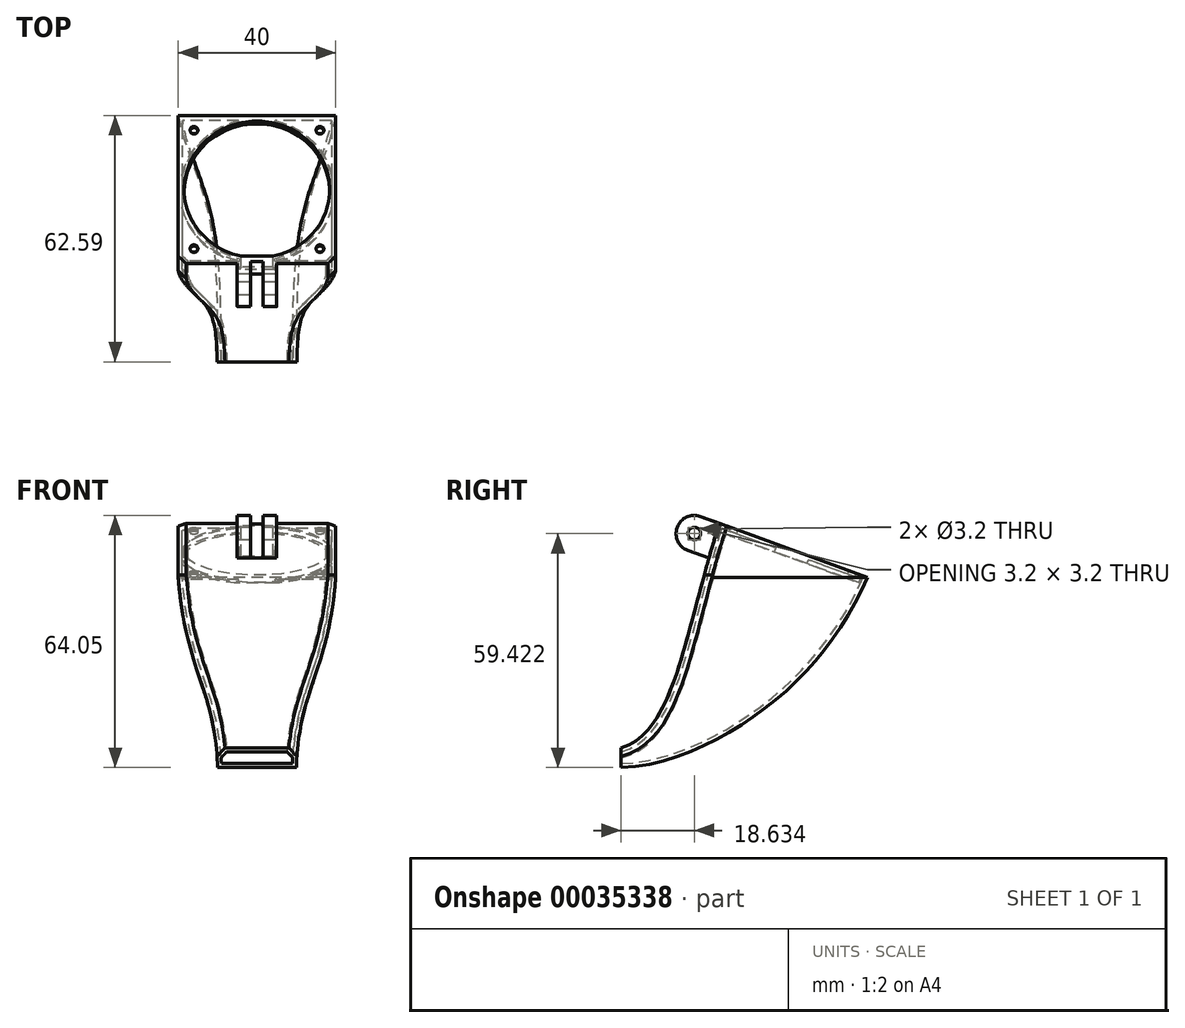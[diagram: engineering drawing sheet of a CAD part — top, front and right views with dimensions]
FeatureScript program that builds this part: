
annotation { "Feature Type Name" : "Feature", "Feature Type Description" : "" }
export const myFeature = defineFeature(function(context is Context, id is Id, definition is map)
    precondition{}
    {
        {
            var Q0;
            Q0=qCreatedBy(makeId("Right.planeOp"),FACE);
            var sketch = newSketch(context, id + "F0", { "sketchPlane" : qUnion([Q0])});
            skLineSegment(sketch, "E0", {"start": v(0, 5) * mm, "end": v(0, 0) * mm});
            skLineSegment(sketch, "E1", {"start": v(62.59, 48.32) * mm, "end": v(25, 62) * mm});
            skFitSpline(sketch, "E2", {"points": [v(62.59, 48.32) * mm, v(0, 0) * mm], "startDerivative": vector(-40.57, -96.87) * mm, "endDerivative": vector(-50.06, 0) * mm});
            skFitSpline(sketch, "E3", {"points": [v(25, 62) * mm, v(0, 5) * mm], "startDerivative": vector(-26.25, -81.63) * mm, "endDerivative": vector(-41.59, -11.88) * mm});
            skSolve(sketch);
        }
        {
            var Q0;
            Q0=qSketchRegion(id+"F0",true);
            extrude(context, id + "F1", {"entities" : qUnion([Q0]), "depth" : 40 * mm, "symmetric" : true});
        }
        {
            var Q0;
            Q0=qCreatedBy(makeId("Front.planeOp"),FACE);
            var sketch = newSketch(context, id + "F2", { "sketchPlane" : qUnion([Q0])});
            skLineSegment(sketch, "E4", {"start": v(10, 0) * mm, "end": v(-10, 0) * mm});
            skLineSegment(sketch, "E5", {"start": v(20, 62) * mm, "end": v(-20, 62) * mm});
            skLineSegment(sketch, "E6", {"start": v(-20, 62) * mm, "end": v(-20, 48.32) * mm});
            skLineSegment(sketch, "E7", {"start": v(20, 62) * mm, "end": v(20, 48.32) * mm});
            skPoint(sketch, "E8", {"position": v(0, 0) * mm});
            skFitSpline(sketch, "E9", {"points": [v(20, 48.32) * mm, v(10, 0) * mm], "startDerivative": vector(-5.16, -71.52) * mm, "endDerivative": vector(-1.89, -60.47) * mm});
            skFitSpline(sketch, "E10.0.MirrorCS", {"points": [v(-20, 48.32) * mm, v(-10, 0) * mm], "startDerivative": vector(5.16, -71.52) * mm, "endDerivative": vector(1.89, -60.47) * mm});
            skSolve(sketch);
        }
        {
            var Q0;
            Q0=qSketchRegion(id+"F2",true);
            var Q1;
            Q1=makeQuery(id+"F1.opExtrude","SWEPT_FACE",FACE,{"disambiguationData":[OSD([sQuery(id+"F0.wireOp",EDGE,"E2")])]});
            extrude(context, id + "F3", {"entities" : qUnion([Q0]), "operationType" : NewBodyOperationType.INTERSECT, "endBound" : BoundingType.UP_TO_BODY, "oppositeDirection" : true, "endBoundEntityBody" : qUnion([Q1]), "depth" : 25 * mm});
        }
        {
            var Q0;
            Q0=makeQuery(id+"F1.opExtrude","SWEPT_FACE",FACE,{"disambiguationData":[OSD([sQuery(id+"F0.wireOp",EDGE,"E1")])]});
            var sketch = newSketch(context, id + "F4", { "sketchPlane" : qUnion([Q0])});
            skLineSegment(sketch, "E11", {"start": v(20, 2.29) * mm, "end": v(-20, 42.29) * mm, "construction": true});
            skLineSegment(sketch, "E12", {"start": v(-20, 2.29) * mm, "end": v(20, 42.29) * mm, "construction": true});
            skCircle(sketch, "E13", {"center": v(0, 22.29) * mm, "radius": 18.5 * mm});
            skSolve(sketch);
        }
        {
            var Q0;
            Q0=qSketchRegion(id+"F4",true);
            extrude(context, id + "F5", {"entities" : qUnion([Q0]), "operationType" : NewBodyOperationType.REMOVE, "oppositeDirection" : true, "depth" : 2 * mm});
        }
        {
            var Q0;
            Q0=makeQuery(id+"F3.boolean.opBoolean","COPY",EDGE,{"derivedFrom":makeQuery(id+"F3.opExtrude","TWEAK_EDGE",EDGE,{"derivedFrom":[makeQuery(id+"F1.opExtrude","SWEPT_FACE",FACE,{"disambiguationData":[OSD([sQuery(id+"F0.wireOp",EDGE,"E2")])]}),makeQuery(id+"F2.imprint","IMPRINT",EDGE,{"derivedFrom":sQuery(id+"F2.wireOp",EDGE,"E9")})]})});
            var Q1;
            Q1=makeQuery(id+"F3.boolean.opBoolean","INTERSECT",EDGE,{"derivedFrom":[makeQuery(id+"F1.opExtrude","SWEPT_FACE",FACE,{"disambiguationData":[OSD([sQuery(id+"F0.wireOp",EDGE,"E3")])]}),makeQuery(id+"F3.opExtrude","SWEPT_FACE",FACE,{"disambiguationData":[OSD([sQuery(id+"F2.wireOp",EDGE,"E9")])]})]});
            var Q2;
            Q2=makeQuery(id+"F1.opExtrude","CAP_EDGE",EDGE,{"disambiguationData":[OSD([sQuery(id+"F0.wireOp",EDGE,"E3")])],"isStart":false});
            var Q3;
            Q3=makeQuery(id+"F3.boolean.opBoolean","INTERSECT",EDGE,{"derivedFrom":[makeQuery(id+"F1.opExtrude","SWEPT_FACE",FACE,{"disambiguationData":[OSD([sQuery(id+"F0.wireOp",EDGE,"E3")])]}),makeQuery(id+"F3.opExtrude","SWEPT_FACE",FACE,{"disambiguationData":[OSD([sQuery(id+"F2.wireOp",EDGE,"E10.0.MirrorCS")])]})]});
            var Q4;
            Q4=makeQuery(id+"F1.opExtrude","CAP_EDGE",EDGE,{"disambiguationData":[OSD([sQuery(id+"F0.wireOp",EDGE,"E3")])],"isStart":true});
            var Q5;
            Q5=makeQuery(id+"F3.boolean.opBoolean","COPY",EDGE,{"derivedFrom":makeQuery(id+"F3.opExtrude","TWEAK_EDGE",EDGE,{"derivedFrom":[makeQuery(id+"F1.opExtrude","SWEPT_FACE",FACE,{"disambiguationData":[OSD([sQuery(id+"F0.wireOp",EDGE,"E2")])]}),makeQuery(id+"F2.imprint","IMPRINT",EDGE,{"derivedFrom":sQuery(id+"F2.wireOp",EDGE,"E10.0.MirrorCS")})]})});
            chamfer(context, id + "F6", {"entities" : qUnion([Q0, Q1, Q2, Q3, Q4, Q5]), "width" : 2 * mm, "tangentPropagation" : true});
        }
        {
            var Q0;
            Q0=makeQuery(id+"F5.boolean.opBoolean","COPY",FACE,{"derivedFrom":makeQuery(id+"F5.opExtrude","CAP_FACE",FACE,{"disambiguationData":[OSD([sQuery(id+"F4.wireOp",EDGE,"E13")])],"isStart":false})});
            var Q1;
            Q1=makeQuery(id+"F1.opExtrude","SWEPT_FACE",FACE,{"disambiguationData":[OSD([sQuery(id+"F0.wireOp",EDGE,"E0")])]});
            shell(context, id + "F7", {"entities" : qUnion([Q0, Q1]), "thickness" : 1 * mm});
        }
        {
            var Q0;
            Q0=makeQuery(id+"F1.opExtrude","SWEPT_FACE",FACE,{"disambiguationData":[OSD([sQuery(id+"F0.wireOp",EDGE,"E1")])]});
            var sketch = newSketch(context, id + "F8", { "sketchPlane" : qUnion([Q0])});
            skCircle(sketch, "E14", {"center": v(16, 38.34) * mm, "radius": 1 * mm});
            skCircle(sketch, "E15", {"center": v(-16, 38.34) * mm, "radius": 1 * mm});
            skCircle(sketch, "E16", {"center": v(-16, 6.34) * mm, "radius": 1 * mm});
            skCircle(sketch, "E17", {"center": v(16, 6.34) * mm, "radius": 1 * mm});
            skPoint(sketch, "E18", {"position": v(-20, 22.34) * mm});
            skSolve(sketch);
        }
        {
            var Q0;
            Q0=qSketchRegion(id+"F8",true);
            var Q1;
            Q1=makeQuery(id+"F7.opShell","OFFSET_FACE",FACE,{"disambiguationData":[OSD([sQuery(id+"F0.wireOp",EDGE,"E1")]),OD(1.0)]});
            extrude(context, id + "F9", {"entities" : qUnion([Q0]), "operationType" : NewBodyOperationType.REMOVE, "endBound" : BoundingType.UP_TO_SURFACE, "oppositeDirection" : true, "endBoundEntityFace" : qUnion([Q1]), "depth" : 25 * mm});
        }
        {
            var Q0;
            Q0=qCreatedBy(makeId("Right.planeOp"),FACE);
            var sketch = newSketch(context, id + "F10", { "sketchPlane" : qUnion([Q0])});
            skLineSegment(sketch, "E19", {"start": v(15.88, 65.32) * mm, "end": v(12.74, 56.67) * mm});
            skLineSegment(sketch, "E20", {"start": v(12.74, 56.67) * mm, "end": v(23.73, 52.67) * mm});
            skLineSegment(sketch, "E21", {"start": v(23.73, 52.67) * mm, "end": v(26.88, 61.32) * mm});
            skLineSegment(sketch, "E22", {"start": v(26.88, 61.32) * mm, "end": v(25, 62) * mm});
            skLineSegment(sketch, "E23", {"start": v(25, 62) * mm, "end": v(25, 62) * mm});
            skLineSegment(sketch, "E24", {"start": v(25, 62) * mm, "end": v(15.88, 65.32) * mm});
            skCircle(sketch, "E25", {"center": v(18.63, 59.42) * mm, "radius": 1.6 * mm});
            skSolve(sketch);
        }
        {
            var Q0;
            Q0=qSketchRegion(id+"F10",true);
            extrude(context, id + "F11", {"entities" : qUnion([Q0]), "operationType" : NewBodyOperationType.ADD, "depth" : 10 * mm, "symmetric" : true});
        }
        {
            var Q0;
            Q0=makeQuery(id+"F11.opExtrude","CAP_EDGE",EDGE,{"disambiguationData":[OSD([sQuery(id+"F10.wireOp",EDGE,"E21")])],"isStart":true});
            var Q1;
            Q1=makeQuery(id+"F11.opExtrude","CAP_EDGE",EDGE,{"disambiguationData":[OSD([sQuery(id+"F10.wireOp",EDGE,"E21")])],"isStart":false});
            var Q2;
            Q2=makeQuery(id+"F11.opExtrude","SWEPT_EDGE",EDGE,{"disambiguationData":[OSD([sQuery(id+"F10.wireOp",EDGE,"E20"),sQuery(id+"F10.wireOp",EDGE,"E21")])]});
            chamfer(context, id + "F12", {"entities" : qUnion([Q0, Q1, Q2]), "width" : 1 * mm, "tangentPropagation" : true});
        }
        {
            var Q0;
            Q0=makeQuery(id+"F11.opExtrude","SWEPT_EDGE",EDGE,{"disambiguationData":[OSD([sQuery(id+"F10.wireOp",EDGE,"E19"),sQuery(id+"F10.wireOp",EDGE,"E20")])]});
            var Q1;
            Q1=makeQuery(id+"F11.opExtrude","SWEPT_EDGE",EDGE,{"disambiguationData":[OSD([sQuery(id+"F10.wireOp",EDGE,"E19"),sQuery(id+"F10.wireOp",EDGE,"E24")])]});
            fillet(context, id + "F13", {"entities" : qUnion([Q0, Q1]), "radius" : 4.5 * mm, "tangentPropagation" : true, "allowEdgeOverflow" : false});
        }
        {
            var Q0;
            {var subQ0=sQuery(id+"F10.wireOp",EDGE,"E20");Q0=makeQuery(id+"F11.boolean.opBoolean","SPLIT",FACE,{"disambiguationData":[TD([makeQuery(id+"F1.opExtrude","SWEPT_FACE",FACE,{"disambiguationData":[OSD([sQuery(id+"F0.wireOp",EDGE,"E3")])]})])],"derivedFrom":makeQuery(id+"F11.opExtrude","SWEPT_FACE",FACE,{"disambiguationData":[OSD([subQ0])]})});}
            var sketch = newSketch(context, id + "F14", { "sketchPlane" : qUnion([Q0])});
            skLineSegment(sketch, "E26.bottom", {"start": v(1.6, 20.97) * mm, "end": v(-1.6, 20.97) * mm});
            skLineSegment(sketch, "E26.top", {"start": v(1.6, -2.8) * mm, "end": v(-1.6, -2.8) * mm});
            skLineSegment(sketch, "E26.left", {"start": v(1.6, 20.97) * mm, "end": v(1.6, -2.8) * mm});
            skLineSegment(sketch, "E26.right", {"start": v(-1.6, 20.97) * mm, "end": v(-1.6, -2.8) * mm});
            skPoint(sketch, "E27", {"position": v(0, 20.97) * mm});
            skSolve(sketch);
        }
        {
            var Q0;
            Q0=qSketchRegion(id+"F14",true);
            var Q1;
            Q1=makeQuery(id+"F11.boolean.opBoolean","MERGE",FACE,{"derivedFrom":[makeQuery(id+"F1.opExtrude","SWEPT_FACE",FACE,{"disambiguationData":[OSD([sQuery(id+"F0.wireOp",EDGE,"E1")])]}),makeQuery(id+"F11.opExtrude","SWEPT_FACE",FACE,{"disambiguationData":[OSD([sQuery(id+"F10.wireOp",EDGE,"E22"),sQuery(id+"F10.wireOp",EDGE,"E24")])]})]});
            extrude(context, id + "F15", {"entities" : qUnion([Q0]), "operationType" : NewBodyOperationType.REMOVE, "endBound" : BoundingType.UP_TO_SURFACE, "oppositeDirection" : true, "endBoundEntityFace" : qUnion([Q1]), "depth" : 25 * mm});
        }
    });
